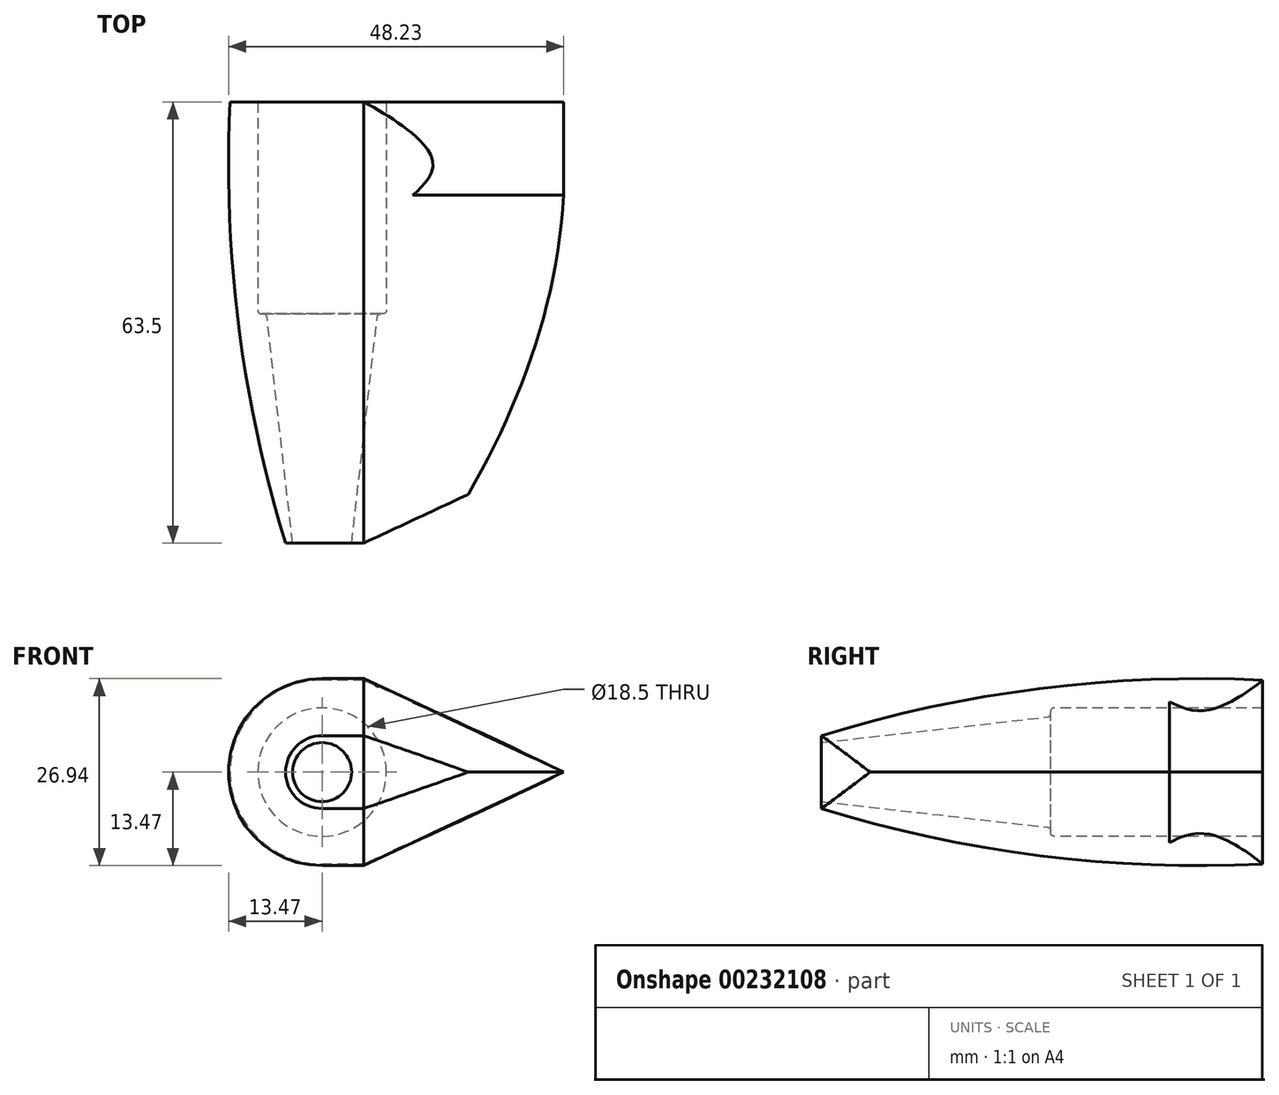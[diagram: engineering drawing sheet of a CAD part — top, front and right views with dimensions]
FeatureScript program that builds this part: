
annotation { "Feature Type Name" : "Feature", "Feature Type Description" : "" }
export const myFeature = defineFeature(function(context is Context, id is Id, definition is map)
    precondition{}
    {
        {
            var Q0;
            Q0=qCreatedBy(makeId("Top.planeOp"),FACE);
            var sketch = newSketch(context, id + "F0", { "sketchPlane" : qUnion([Q0])});
            skLineSegment(sketch, "E0", {"start": v(0, 0) * mm, "end": v(4.25, 0) * mm, "construction": true});
            skLineSegment(sketch, "E1", {"start": v(4.25, 0) * mm, "end": v(5.25, 0) * mm});
            skLineSegment(sketch, "E2", {"start": v(4.25, 0) * mm, "end": v(4.25, 33) * mm, "construction": true});
            skLineSegment(sketch, "E3", {"start": v(4.74, 33) * mm, "end": v(7.99, 33) * mm, "construction": true});
            skLineSegment(sketch, "E4", {"start": v(8.43, 33) * mm, "end": v(8.75, 33) * mm});
            skLineSegment(sketch, "E5", {"start": v(7.94, 32.56) * mm, "end": v(4.25, 0) * mm});
            skLineSegment(sketch, "E6", {"start": v(0, 33) * mm, "end": v(9.25, 33) * mm, "construction": true});
            skPoint(sketch, "E6.endSnap0", {"position": v(9.2, 33) * mm});
            skLineSegment(sketch, "E7", {"start": v(9.25, 33.5) * mm, "end": v(9.25, 63.5) * mm});
            skLineSegment(sketch, "E8", {"start": v(9.25, 63.5) * mm, "end": v(13.25, 63.5) * mm});
            skPoint(sketch, "E9.visualSharp", {"position": v(9.25, 33) * mm});
            skArc(sketch, "E9.filletArc", {"start": v(8.75, 33) * mm, "mid": v(9.1, 33.15) * mm, "end": v(9.25, 33.5) * mm});
            skPoint(sketch, "E10.visualSharp", {"position": v(7.99, 33) * mm});
            skArc(sketch, "E10.filletArc", {"start": v(8.43, 33) * mm, "mid": v(8.1, 32.87) * mm, "end": v(7.94, 32.56) * mm});
            skLineSegment(sketch, "E11", {"start": v(0, 0) * mm, "end": v(0, 65) * mm, "construction": true});
            skArc(sketch, "E12", {"start": v(5.25, 0) * mm, "mid": v(12.02, 31.4) * mm, "end": v(13.25, 63.5) * mm});
            skSolve(sketch);
        }
        {
            var Q0;
            Q0=makeQuery(id+"F0.imprint","IMPRINT",FACE,{"disambiguationData":[TD([[makeQuery(id+"F0.imprint","IMPRINT",EDGE,{"derivedFrom":sQuery(id+"F0.wireOp",EDGE,"E1")}),1.0]])]});
            var Q1;
            Q1=sQuery(id+"F0.wireOp",EDGE,"E11");
            revolve(context, id + "F1", {"entities" : qUnion([Q0]), "axis" : qUnion([Q1]), "revolveType" : RevolveType.FULL});
        }
        {
            var Q0;
            Q0=qCreatedBy(makeId("Right.planeOp"),FACE);
            var sketch = newSketch(context, id + "F2", { "sketchPlane" : qUnion([Q0])});
            skArc(sketch, "E13", {"start": v(0, -5.25) * mm, "mid": v(31.4, -12.02) * mm, "end": v(63.5, -13.25) * mm});
            skArc(sketch, "E14", {"start": v(63.5, 13.25) * mm, "mid": v(31.4, 12.02) * mm, "end": v(0, 5.25) * mm});
            skLineSegment(sketch, "E15", {"start": v(0, 5.25) * mm, "end": v(0, -5.25) * mm});
            skLineSegment(sketch, "E16", {"start": v(63.5, 13.25) * mm, "end": v(63.5, -13.25) * mm});
            skSolve(sketch);
        }
        {
            var Q0;
            Q0 = qSketchRegion(id + "F2", true);
            extrude(context, id + "F3", {"entities" : qUnion([Q0]), "operationType" : NewBodyOperationType.ADD, "depth" : 6 * mm});
        }
        {
            var Q0;
            {var subQ0=sQuery(id+"F2.wireOp",EDGE,"E14");var subQ1=sQuery(id+"F2.wireOp",EDGE,"E13");var subQ2=sQuery(id+"F2.wireOp",EDGE,"E15");var subQ3=sQuery(id+"F2.wireOp",EDGE,"E16");Q0=makeQuery(id+"F3.boolean.opBoolean","SPLIT",FACE,{"disambiguationData":[TD([makeQuery(id+"F1.opRevolve","SWEPT_FACE",FACE,{"disambiguationData":[OSD([sQuery(id+"F0.wireOp",EDGE,"E1")])]})])],"derivedFrom":makeQuery(id+"F3.opExtrude","CAP_FACE",FACE,{"disambiguationData":[OSD([subQ1,subQ0,subQ2,subQ3])],"isStart":false})});}
            var sketch = newSketch(context, id + "F4", { "sketchPlane" : qUnion([Q0])});
            skArc(sketch, "E17", {"start": v(63.5, 13.25) * mm, "mid": v(31.4, 12.02) * mm, "end": v(0, 5.25) * mm});
            skLineSegment(sketch, "E18", {"start": v(0, 5.25) * mm, "end": v(0, -5.25) * mm});
            skArc(sketch, "E19", {"start": v(0, -5.25) * mm, "mid": v(31.4, -12.02) * mm, "end": v(63.5, -13.25) * mm});
            skLineSegment(sketch, "E20", {"start": v(63.5, 13.25) * mm, "end": v(63.5, -13.25) * mm});
            skSolve(sketch);
        }
        {
            var Q0;
            Q0 = qSketchRegion(id + "F4", true);
            extrude(context, id + "F5", {"entities" : qUnion([Q0]), "operationType" : NewBodyOperationType.ADD, "depth" : 40 * mm, "hasDraft" : true, "draftAngle" : 25 * degree, "draftPullDirection" : true});
        }
        {
            var Q0;
            Q0=makeQuery(id+"F3.boolean.opBoolean","MERGE",FACE,{"derivedFrom":[makeQuery(id+"F1.opRevolve","SWEPT_FACE",FACE,{"disambiguationData":[OSD([sQuery(id+"F0.wireOp",EDGE,"E8")])]}),makeQuery(id+"F3.opExtrude","SWEPT_FACE",FACE,{"disambiguationData":[OSD([sQuery(id+"F2.wireOp",EDGE,"E16")])]})]});
            var sketch = newSketch(context, id + "F6", { "sketchPlane" : qUnion([Q0])});
            skFitSpline(sketch, "E21.0.3", {"points": [v(-6, 13.25) * mm, v(-15.64, 8.97) * mm, v(-25.23, 4.56) * mm, v(-34.76, 0) * mm]});
            skFitSpline(sketch, "E21.0.4", {"points": [v(-34.76, 0) * mm, v(-25.23, -4.56) * mm, v(-15.64, -8.97) * mm, v(-6, -13.25) * mm]});
            skPoint(sketch, "E21.0.2.start.orphan", {"position": v(-6, 11.81) * mm});
            skPoint(sketch, "E21.0.0.end.orphan", {"position": v(-6, -11.81) * mm});
            skLineSegment(sketch, "E22", {"start": v(-6, 13.25) * mm, "end": v(-6, -13.25) * mm});
            skSolve(sketch);
        }
        {
            var Q0;
            Q0 = qSketchRegion(id + "F6", true);
            extrude(context, id + "F7", {"entities" : qUnion([Q0]), "operationType" : NewBodyOperationType.ADD, "oppositeDirection" : true, "depth" : 13.4 * mm});
        }
        {
            var Q0;
            Q0=makeQuery(id+"F3.opExtrude","CAP_FACE",FACE,{"disambiguationData":[OSD([sQuery(id+"F2.wireOp",EDGE,"E13"),sQuery(id+"F2.wireOp",EDGE,"E14"),sQuery(id+"F2.wireOp",EDGE,"E15"),sQuery(id+"F2.wireOp",EDGE,"E16")])],"isStart":true});
            var sketch = newSketch(context, id + "F8", { "sketchPlane" : qUnion([Q0])});
            skLineSegment(sketch, "E23.0.0", {"start": v(-63.5, 9.25) * mm, "end": v(-63.5, 0) * mm});
            skLineSegment(sketch, "E23.0.6", {"start": v(0, 0) * mm, "end": v(0, 4.25) * mm});
            skLineSegment(sketch, "E23.0.7", {"start": v(0, 4.25) * mm, "end": v(-32.56, 7.94) * mm});
            skArc(sketch, "E23.0.8", {"start": v(-33, 8.43) * mm, "mid": v(-32.87, 8.1) * mm, "end": v(-32.56, 7.94) * mm});
            skLineSegment(sketch, "E23.0.9", {"start": v(-33, 8.43) * mm, "end": v(-33, 8.75) * mm});
            skArc(sketch, "E23.0.10", {"start": v(-33, 8.75) * mm, "mid": v(-33.15, 9.1) * mm, "end": v(-33.5, 9.25) * mm});
            skLineSegment(sketch, "E23.0.11", {"start": v(-33.5, 9.25) * mm, "end": v(-63.5, 9.25) * mm});
            skLineSegment(sketch, "E24", {"start": v(0, 0) * mm, "end": v(-63.5, 0) * mm});
            skPoint(sketch, "E23.0.1.start.orphan", {"position": v(-63.5, -9.25) * mm});
            skPoint(sketch, "E23.0.2.start.orphan", {"position": v(-33.5, -9.25) * mm});
            skPoint(sketch, "E23.0.3.end.orphan", {"position": v(-33, -8.43) * mm});
            skPoint(sketch, "E23.0.3.start.orphan", {"position": v(-33, -8.75) * mm});
            skPoint(sketch, "E23.0.5.start.orphan", {"position": v(-32.56, -7.94) * mm});
            skPoint(sketch, "E25.orphan", {"position": v(0, -4.25) * mm});
            skSolve(sketch);
        }
        {
            var Q0;
            Q0=makeQuery(id+"F8.imprint","IMPRINT",FACE,{"disambiguationData":[TD([[makeQuery(id+"F8.imprint","IMPRINT",EDGE,{"derivedFrom":sQuery(id+"F8.wireOp",EDGE,"E23.0.0")}),1.0]])]});
            var Q1;
            Q1=sQuery(id+"F8.wireOp",EDGE,"E24");
            revolve(context, id + "F9", {"operationType" : NewBodyOperationType.REMOVE, "entities" : qUnion([Q0]), "axis" : qUnion([Q1]), "revolveType" : RevolveType.FULL, "oppositeDirection" : true});
        }
    });
